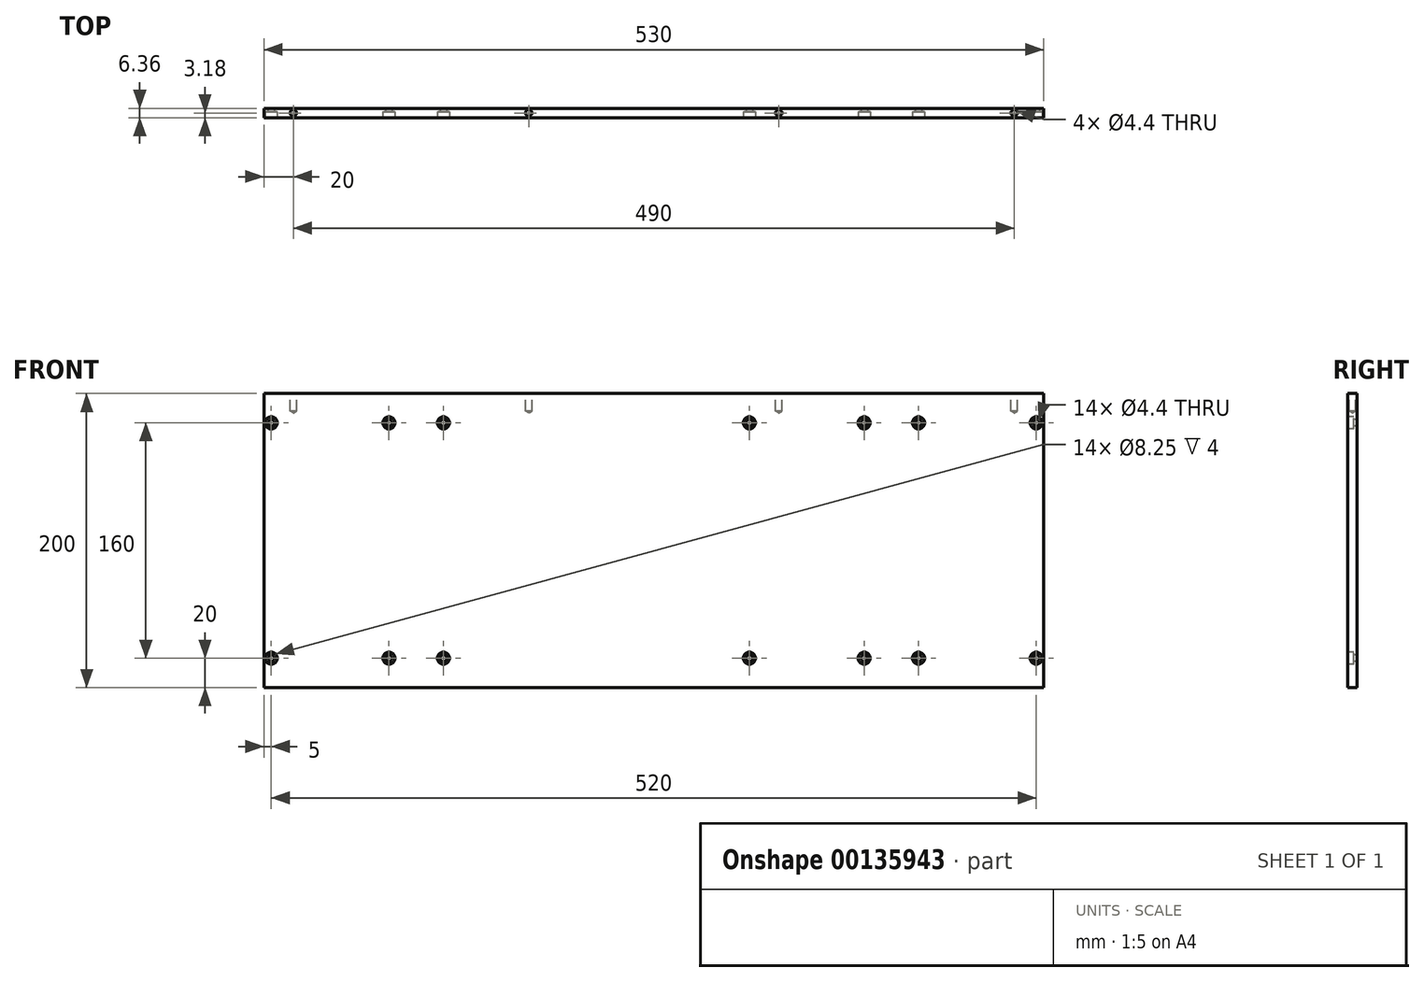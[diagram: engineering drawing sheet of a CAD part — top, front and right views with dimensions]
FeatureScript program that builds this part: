
annotation { "Feature Type Name" : "Feature", "Feature Type Description" : "" }
export const myFeature = defineFeature(function(context is Context, id is Id, definition is map)
    precondition{}
    {
        {
            var Q0;
            Q0=qCreatedBy(makeId("Front.planeOp"),FACE);
            var sketch = newSketch(context, id + "F0", { "sketchPlane" : qUnion([Q0])});
            skLineSegment(sketch, "E0.bottom", {"start": v(265, -100) * mm, "end": v(-265, -100) * mm});
            skLineSegment(sketch, "E0.top", {"start": v(265, 100) * mm, "end": v(-265, 100) * mm});
            skLineSegment(sketch, "E0.left", {"start": v(265, -100) * mm, "end": v(265, 100) * mm});
            skLineSegment(sketch, "E0.right", {"start": v(-265, -100) * mm, "end": v(-265, 100) * mm});
            skPoint(sketch, "E0.middle", {"position": v(0, 0) * mm});
            skSolve(sketch);
        }
        {
            var Q0;
            Q0=makeQuery(id+"F0.imprint","IMPRINT",FACE,{"disambiguationData":[TD([[makeQuery(id+"F0.imprint","IMPRINT",EDGE,{"derivedFrom":sQuery(id+"F0.wireOp",EDGE,"E0.bottom")}),-1.0]])]});
            extrude(context, id + "F1", {"entities" : qUnion([Q0]), "endBound" : BoundingType.SYMMETRIC, "depth" : 6.35 * mm});
        }
        {
            var Q0;
            Q0=makeQuery(id+"F1.opExtrude","SWEPT_FACE",FACE,{"disambiguationData":[OSD([sQuery(id+"F0.wireOp",EDGE,"E0.top")])]});
            var sketch = newSketch(context, id + "F2", { "sketchPlane" : qUnion([Q0])});
            skCircle(sketch, "E1", {"center": v(-245, 0) * mm, "radius": 2 * mm});
            skCircle(sketch, "E2.MirrorC", {"center": v(245, 0) * mm, "radius": 2 * mm});
            skCircle(sketch, "E3", {"center": v(-85, 0) * mm, "radius": 2 * mm});
            skCircle(sketch, "E4.MirrorC", {"center": v(85, 0) * mm, "radius": 2 * mm});
            skSolve(sketch);
        }
        {
            var Q0;
            Q0=sQuery(id+"F2.wireOp",VERTEX,"E1.center");
            var Q1;
            Q1=sQuery(id+"F2.wireOp",VERTEX,"T9IXx7JC-zBGf-hUYm-T3yX-14epucO03qIy.center");
            var Q2;
            Q2=sQuery(id+"F2.wireOp",VERTEX,"N0LrrZqT-inZq-m3Pn-OrCf-dQQlCZNRCZq6.center");
            var Q3;
            Q3=sQuery(id+"FIcnoNRWDtXQDt8_1.wireOp",VERTEX,"3cPgaEPO-l2S4-59tO-MI0H-XOzf9UvMpscF.center");
            var Q4;
            Q4=sQuery(id+"FIcnoNRWDtXQDt8_1.wireOp",VERTEX,"TkyO21D5-myKt-kctF-Qau4-7kkSpgJoDvGR.center");
            var Q5;
            Q5=sQuery(id+"FIcnoNRWDtXQDt8_1.wireOp",VERTEX,"d543fb3c-15d2-46c5-8e42-b8e89170ded70.MirrorC.center");
            var Q6;
            Q6=sQuery(id+"F2.wireOp",VERTEX,"FNoEuDts-k7e2-Ixns-EDq3-ArStTqx777KW.center");
            var Q7;
            Q7=sQuery(id+"F2.wireOp",VERTEX,"E2.MirrorC.center");
            var Q8;
            Q8=sQuery(id+"F2.wireOp",VERTEX,"E3.center");
            var Q9;
            Q9=sQuery(id+"F2.wireOp",VERTEX,"E4.MirrorC.center");
            var Q10;
            Q10=sQuery(id+"FIcnoNRWDtXQDt8_1.wireOp",VERTEX,"g584gUje-TA9k-HtRv-aNsc-8fThQo474qbw.center");
            var Q11;
            Q11=sQuery(id+"FIcnoNRWDtXQDt8_1.wireOp",VERTEX,"6a3e9595-9a16-4d97-9c0c-f3d9127132c10.MirrorC.center");
            var Q12;
            Q12=makeQuery(id+"F1.opExtrude","SWEPT_BODY",BODY,{"disambiguationData":[OSD([sQuery(id+"F0.wireOp",EDGE,"E0.bottom"),sQuery(id+"F0.wireOp",EDGE,"E0.top"),sQuery(id+"F0.wireOp",EDGE,"E0.left"),sQuery(id+"F0.wireOp",EDGE,"E0.right"),sQuery(id+"F0.wireOp",EDGE,"XWZrsFJl-hZ8c-8RFI-7IJq-EzOZ3sIGLfD4"),sQuery(id+"F0.wireOp",EDGE,"QB0C6CPn-qOL8-fIRA-QjEU-Y9BwwvSa6pRB"),sQuery(id+"F0.wireOp",EDGE,"G4GAvN2Z-Aj42-7Is6-4Fkr-iGkbHWXBV4Qq"),sQuery(id+"F0.wireOp",EDGE,"ztsScnvx-69nE-OQe9-Xu7z-F3aSEwL5bO77"),sQuery(id+"F0.wireOp",EDGE,"QAZC7S4a-mdPt-mVvo-yF0x-VzN3XJBQlE6b"),sQuery(id+"F0.wireOp",EDGE,"MX8Ww9h4-DqsU-lgLO-alZj-Cp6TfRqocJF7")])]});
            hole(context, id + "F3", {"style" : HoleStyle.SIMPLE, "endStyle" : HoleEndStyle.BLIND, "standardTappedOrClearance" : lookupTablePath({ "standard" : "ISO", "fit" : "Normal", "size" : "M4", "type" : "Clearance" }), "standardBlindInLast" : lookupTablePath({ "fit" : "Standard", "standard" : "ISO", "size" : "M4", "type" : "Clearance" }), "holeDiameter" : 4.4 * mm, "holeDepth" : 12 * mm, "locations" : qUnion([Q0, Q1, Q2, Q3, Q4, Q5, Q6, Q7, Q8, Q9, Q10, Q11]), "scope" : qUnion([Q12])});
        }
        {
            var Q0;
            Q0=makeQuery(id+"F1.opExtrude","CAP_FACE",FACE,{"disambiguationData":[OSD([sQuery(id+"F0.wireOp",EDGE,"E0.bottom"),sQuery(id+"F0.wireOp",EDGE,"E0.top"),sQuery(id+"F0.wireOp",EDGE,"E0.left"),sQuery(id+"F0.wireOp",EDGE,"E0.right")])],"isStart":false});
            var sketch = newSketch(context, id + "F4", { "sketchPlane" : qUnion([Q0])});
            skCircle(sketch, "E5", {"center": v(-260, -80) * mm, "radius": 2 * mm});
            skCircle(sketch, "E6", {"center": v(-260, 80) * mm, "radius": 2 * mm});
            skCircle(sketch, "E7", {"center": v(180, -80) * mm, "radius": 2 * mm});
            skCircle(sketch, "E8", {"center": v(180, 80) * mm, "radius": 2 * mm});
            skCircle(sketch, "E9", {"center": v(-143, -80) * mm, "radius": 2.5 * mm});
            skCircle(sketch, "E10.MirrorC", {"center": v(-143, 80) * mm, "radius": 2.5 * mm});
            skCircle(sketch, "E11.MirrorC", {"center": v(143, -80) * mm, "radius": 2.5 * mm});
            skCircle(sketch, "E12.MirrorC", {"center": v(143, 80) * mm, "radius": 2.5 * mm});
            skCircle(sketch, "E13", {"center": v(65, -80) * mm, "radius": 2.5 * mm});
            skCircle(sketch, "E14.MirrorC", {"center": v(65, 80) * mm, "radius": 2.5 * mm});
            skCircle(sketch, "E15.MirrorC", {"center": v(-65, 80) * mm, "radius": 2.5 * mm});
            skCircle(sketch, "E16.MirrorC", {"center": v(-65, -80) * mm, "radius": 2.5 * mm});
            skCircle(sketch, "E17.MirrorC", {"center": v(260, -80) * mm, "radius": 2 * mm});
            skCircle(sketch, "E18.MirrorC", {"center": v(260, 80) * mm, "radius": 2 * mm});
            skCircle(sketch, "E19.MirrorC", {"center": v(-180, -80) * mm, "radius": 2 * mm});
            skCircle(sketch, "E20.MirrorC", {"center": v(-180, 80) * mm, "radius": 2 * mm});
            skSolve(sketch);
        }
        {
            var Q0;
            Q0=sQuery(id+"F4.wireOp",VERTEX,"03CLBzXD-TyXJ-dOCx-ZrAg-tilGR4lqWcCv.center");
            var Q1;
            Q1=sQuery(id+"F4.wireOp",VERTEX,"E6.center");
            var Q2;
            Q2=sQuery(id+"F4.wireOp",VERTEX,"E5.center");
            var Q3;
            Q3=sQuery(id+"F4.wireOp",VERTEX,"E7.center");
            var Q4;
            Q4=sQuery(id+"F4.wireOp",VERTEX,"E8.center");
            var Q5;
            Q5=sQuery(id+"F4.wireOp",VERTEX,"oYJsDZwO-tQaO-SiK6-l9vp-6JT4rw1mrPIV.center");
            var Q6;
            Q6=sQuery(id+"F4.wireOp",VERTEX,"E9.center");
            var Q7;
            Q7=sQuery(id+"F4.wireOp",VERTEX,"E10.MirrorC.center");
            var Q8;
            Q8=sQuery(id+"F4.wireOp",VERTEX,"E11.MirrorC.center");
            var Q9;
            Q9=sQuery(id+"F4.wireOp",VERTEX,"E12.MirrorC.center");
            var Q10;
            Q10=sQuery(id+"F4.wireOp",VERTEX,"E13.center");
            var Q11;
            Q11=sQuery(id+"F4.wireOp",VERTEX,"E14.MirrorC.center");
            var Q12;
            Q12=sQuery(id+"F4.wireOp",VERTEX,"E15.MirrorC.center");
            var Q13;
            Q13=sQuery(id+"F4.wireOp",VERTEX,"E16.MirrorC.center");
            var Q14;
            Q14=sQuery(id+"F4.wireOp",VERTEX,"E18.MirrorC.center");
            var Q15;
            Q15=sQuery(id+"F4.wireOp",VERTEX,"E17.MirrorC.center");
            var Q16;
            Q16=sQuery(id+"F4.wireOp",VERTEX,"E20.MirrorC.center");
            var Q17;
            Q17=sQuery(id+"F4.wireOp",VERTEX,"E19.MirrorC.center");
            var Q18;
            Q18=makeQuery(id+"F1.opExtrude","SWEPT_BODY",BODY,{"disambiguationData":[OSD([sQuery(id+"F0.wireOp",EDGE,"E0.bottom"),sQuery(id+"F0.wireOp",EDGE,"E0.top"),sQuery(id+"F0.wireOp",EDGE,"E0.left"),sQuery(id+"F0.wireOp",EDGE,"E0.right")])]});
            hole(context, id + "F5", {"style" : HoleStyle.C_BORE, "endStyle" : HoleEndStyle.BLIND, "standardTappedOrClearance" : lookupTablePath({ "standard" : "ISO", "fit" : "Normal", "size" : "M4", "type" : "Clearance" }), "standardBlindInLast" : lookupTablePath({ "fit" : "Standard", "standard" : "ISO", "size" : "M4", "type" : "Clearance" }), "holeDiameter" : 4.4 * mm, "cBoreDiameter" : 8.25 * mm, "cBoreDepth" : 4 * mm, "holeDepth" : 10 * mm, "startFromSketch" : true, "locations" : qUnion([Q0, Q1, Q2, Q3, Q4, Q5, Q6, Q7, Q8, Q9, Q10, Q11, Q12, Q13, Q14, Q15, Q16, Q17]), "scope" : qUnion([Q18])});
        }
    });
